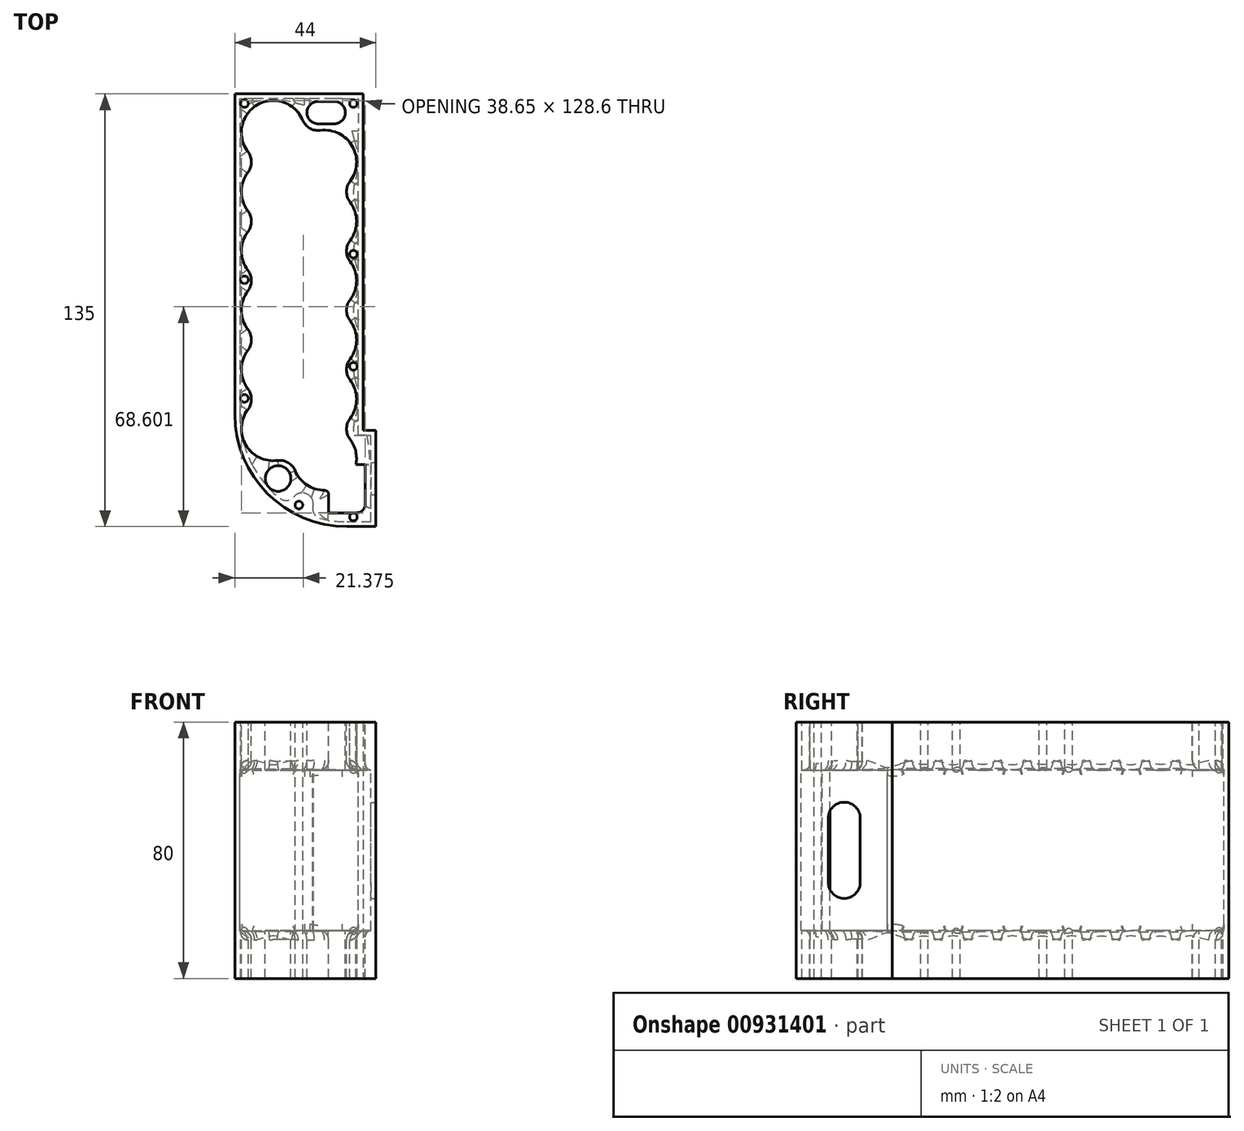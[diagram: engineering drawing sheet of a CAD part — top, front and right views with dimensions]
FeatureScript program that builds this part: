
annotation { "Feature Type Name" : "Feature", "Feature Type Description" : "" }
export const myFeature = defineFeature(function(context is Context, id is Id, definition is map)
    precondition{}
    {
        {
            var Q0;
            Q0=qCreatedBy(makeId("Top.planeOp"),FACE);
            cPlane(context, id + "F0", {"entities" : qUnion([Q0]), "cplaneType" : CPlaneType.OFFSET, "offset" : 40 * mm, "width" : 150 * mm, "height" : 150 * mm});
        }
        {
            var Q0;
            Q0=qCreatedBy(makeId("Top.planeOp"),FACE);
            var sketch = newSketch(context, id + "F1", { "sketchPlane" : qUnion([Q0])});
            skLineSegment(sketch, "E0.right", {"start": v(-40, 0) * mm, "end": v(-40, -100) * mm});
            skPoint(sketch, "E1.visualSharp", {"position": v(-40, -135) * mm});
            skPoint(sketch, "E2.visualSharp", {"position": v(-40, 0) * mm});
            skLineSegment(sketch, "E3", {"start": v(0, 0) * mm, "end": v(0, -105) * mm});
            skLineSegment(sketch, "E4", {"start": v(-40, 0) * mm, "end": v(0, 0) * mm});
            skLineSegment(sketch, "E5.top", {"start": v(0, -105) * mm, "end": v(4, -105) * mm});
            skLineSegment(sketch, "E5.right", {"start": v(4, -135) * mm, "end": v(4, -105) * mm});
            skLineSegment(sketch, "E6", {"start": v(4, -135) * mm, "end": v(-5, -135) * mm});
            skArc(sketch, "E7.filletArc", {"start": v(-40, -100) * mm, "mid": v(-29.75, -124.75) * mm, "end": v(-5, -135) * mm});
            skSolve(sketch);
        }
        {
            var Q0;
            Q0=makeQuery(id+"F1.imprint","IMPRINT",FACE,{"disambiguationData":[TD([[makeQuery(id+"F1.imprint","IMPRINT",EDGE,{"derivedFrom":sQuery(id+"F1.wireOp",EDGE,"E0.right")}),1.0]])]});
            extrude(context, id + "F2", {"entities" : qUnion([Q0]), "depth" : 80 * mm, "offsetDistance" : 25 * mm});
        }
        {
            var Q0;
            Q0=makeQuery(id+"F2.opExtrude","CAP_FACE",FACE,{"disambiguationData":[OSD([sQuery(id+"F1.wireOp",EDGE,"E0.top"),sQuery(id+"F1.wireOp",EDGE,"E0.left"),sQuery(id+"F1.wireOp",EDGE,"E0.right"),sQuery(id+"F1.wireOp",EDGE,"E1.filletArc"),sQuery(id+"F1.wireOp",EDGE,"5de082b1-88c5-4f56-9cd1-09331b00fd2d.trimOffspring"),sQuery(id+"F1.wireOp",EDGE,"y3ADj3GU-friW-LrWS-ZnVf-nILArbpNqqxh"),sQuery(id+"F1.wireOp",EDGE,"uJFoRx8a-Ppp5-qDHF-xN9b-6GK6148I28lK.left"),sQuery(id+"F1.wireOp",EDGE,"uJFoRx8a-Ppp5-qDHF-xN9b-6GK6148I28lK.right"),sQuery(id+"F1.wireOp",EDGE,"b2af3c1e-7181-4fb0-8f65-0e7276eb82ca.trimOffspring"),sQuery(id+"F1.wireOp",EDGE,"7f23342a-69af-42d1-8bd4-2c05ba6568f0.filletArc"),sQuery(id+"F1.wireOp",EDGE,"185a892e-41b9-4107-83af-0d2bc894ce6d.filletArc"),sQuery(id+"F1.wireOp",EDGE,"b194760c-3b3b-4794-9b8b-2c71253df791.filletArc"),sQuery(id+"F1.wireOp",EDGE,"319700d8-119a-4906-a10f-a42b0ff3433d.filletArc"),sQuery(id+"F1.wireOp",EDGE,"ZXkUyEPo-FX4a-Sv19-M192-gNO29ZRSfF8I"),sQuery(id+"F1.wireOp",EDGE,"HvNRA3BX-9FXn-12fZ-Fs24-gRpAAjMtZzFk")])],"isStart":false});
            var sketch = newSketch(context, id + "F3", { "sketchPlane" : qUnion([Q0])});
            skLineSegment(sketch, "E8.2", {"start": v(-37, 0) * mm, "end": v(-37, -100) * mm, "construction": true});
            skPoint(sketch, "E9", {"position": v(-37, -3) * mm});
            skPoint(sketch, "E10", {"position": v(-20, -128.27) * mm});
            skPoint(sketch, "E11", {"position": v(-3, -132) * mm});
            skLineSegment(sketch, "E12.0", {"start": v(-3, 0) * mm, "end": v(-3, -135) * mm, "construction": true});
            skPoint(sketch, "E13", {"position": v(-3, -85) * mm});
            skPoint(sketch, "E14", {"position": v(-3, -50) * mm});
            skPoint(sketch, "E15", {"position": v(-3, -3) * mm});
            skPoint(sketch, "E16", {"position": v(-37, -95) * mm});
            skPoint(sketch, "E17", {"position": v(-37, -58) * mm});
            skArc(sketch, "E18.0", {"start": v(-37, -100) * mm, "mid": v(-27.63, -122.63) * mm, "end": v(-5, -132) * mm, "construction": true});
            skSolve(sketch);
        }
        {
            var Q0;
            Q0=sQuery(id+"F3.wireOp",VERTEX,"E9");
            var Q1;
            Q1=sQuery(id+"F3.wireOp",VERTEX,"f4559d67-b2ce-4cbe-8c48-f7303b728956.direction1.end");
            var Q2;
            Q2=sQuery(id+"F3.wireOp",VERTEX,"666fff49-049b-4152-8810-0d37dc0279b3");
            var Q3;
            Q3=sQuery(id+"F3.wireOp",VERTEX,"E10");
            var Q4;
            Q4=sQuery(id+"F3.wireOp",VERTEX,"E11");
            var Q5;
            Q5=sQuery(id+"F3.wireOp",VERTEX,"E13");
            var Q6;
            Q6=sQuery(id+"F3.wireOp",VERTEX,"E14");
            var Q7;
            Q7=sQuery(id+"F3.wireOp",VERTEX,"E15");
            var Q8;
            Q8=sQuery(id+"F3.wireOp",VERTEX,"E17");
            var Q9;
            Q9=sQuery(id+"F3.wireOp",VERTEX,"E16");
            var Q10;
            Q10=makeQuery(id+"F2.opExtrude","SWEPT_BODY",BODY,{"disambiguationData":[OSD([sQuery(id+"F1.wireOp",EDGE,"E0.top"),sQuery(id+"F1.wireOp",EDGE,"E0.left"),sQuery(id+"F1.wireOp",EDGE,"E0.right"),sQuery(id+"F1.wireOp",EDGE,"E1.filletArc"),sQuery(id+"F1.wireOp",EDGE,"5de082b1-88c5-4f56-9cd1-09331b00fd2d.trimOffspring"),sQuery(id+"F1.wireOp",EDGE,"y3ADj3GU-friW-LrWS-ZnVf-nILArbpNqqxh"),sQuery(id+"F1.wireOp",EDGE,"uJFoRx8a-Ppp5-qDHF-xN9b-6GK6148I28lK.left"),sQuery(id+"F1.wireOp",EDGE,"uJFoRx8a-Ppp5-qDHF-xN9b-6GK6148I28lK.right"),sQuery(id+"F1.wireOp",EDGE,"b2af3c1e-7181-4fb0-8f65-0e7276eb82ca.trimOffspring"),sQuery(id+"F1.wireOp",EDGE,"7f23342a-69af-42d1-8bd4-2c05ba6568f0.filletArc"),sQuery(id+"F1.wireOp",EDGE,"185a892e-41b9-4107-83af-0d2bc894ce6d.filletArc"),sQuery(id+"F1.wireOp",EDGE,"b194760c-3b3b-4794-9b8b-2c71253df791.filletArc"),sQuery(id+"F1.wireOp",EDGE,"319700d8-119a-4906-a10f-a42b0ff3433d.filletArc"),sQuery(id+"F1.wireOp",EDGE,"ZXkUyEPo-FX4a-Sv19-M192-gNO29ZRSfF8I"),sQuery(id+"F1.wireOp",EDGE,"HvNRA3BX-9FXn-12fZ-Fs24-gRpAAjMtZzFk")])]});
            hole(context, id + "F4", {"style" : HoleStyle.SIMPLE, "endStyle" : HoleEndStyle.THROUGH, "holeDiameter" : 2.4 * mm, "majorDiameter" : 5 * mm, "isTappedThrough" : true, "tappedDepth" : 12 * mm, "tapClearance" : 3, "locations" : qUnion([Q0, Q1, Q2, Q3, Q4, Q5, Q6, Q7, Q8, Q9]), "scope" : qUnion([Q10])});
        }
        {
            var Q0;
            Q0=makeQuery(id+"F3.imprint","IMPRINT",FACE,{"disambiguationData":[TD([[makeQuery(id+"F3.imprint","IMPRINT",EDGE,{"derivedFrom":makeQuery(id+"F2.opExtrude","CAP_EDGE",EDGE,{"disambiguationData":[OSD([sQuery(id+"F1.wireOp",EDGE,"E0.right")])],"isStart":false})}),1.0]])]});
            var sketch = newSketch(context, id + "F5", { "sketchPlane" : qUnion([Q0])});
            skArc(sketch, "E19", {"start": v(-19.46, -8.44) * mm, "mid": v(-32.62, -3.99) * mm, "end": v(-35.35, -17.61) * mm});
            skArc(sketch, "E20.1.0.0", {"start": v(-35.35, -24.89) * mm, "mid": v(-37.25, -30.5) * mm, "end": v(-35.35, -36.11) * mm});
            skArc(sketch, "E20.2.0.0", {"start": v(-35.35, -43.39) * mm, "mid": v(-37.25, -49) * mm, "end": v(-35.35, -54.61) * mm});
            skArc(sketch, "E20.3.0.0", {"start": v(-35.35, -61.89) * mm, "mid": v(-37.25, -67.5) * mm, "end": v(-35.35, -73.11) * mm});
            skArc(sketch, "E20.4.0.0", {"start": v(-35.35, -80.39) * mm, "mid": v(-37.25, -86) * mm, "end": v(-35.35, -91.61) * mm});
            skArc(sketch, "E20.5.0.0", {"start": v(-35.35, -98.89) * mm, "mid": v(-36.01, -109.12) * mm, "end": v(-26.82, -113.67) * mm});
            skLineSegment(sketch, "E20.direction1", {"start": v(-28, -12) * mm, "end": v(-28, -30.5) * mm, "construction": true});
            skArc(sketch, "E21", {"start": v(-4.62, -26.86) * mm, "mid": v(-3.97, -16.62) * mm, "end": v(-13.16, -12.08) * mm});
            skArc(sketch, "E22.1.0.0", {"start": v(-4.62, -45.36) * mm, "mid": v(-2.73, -39.75) * mm, "end": v(-4.62, -34.14) * mm});
            skArc(sketch, "E22.2.0.0", {"start": v(-4.62, -63.86) * mm, "mid": v(-2.73, -58.25) * mm, "end": v(-4.62, -52.64) * mm});
            skArc(sketch, "E22.3.0.0", {"start": v(-4.62, -82.36) * mm, "mid": v(-2.73, -76.75) * mm, "end": v(-4.62, -71.14) * mm});
            skArc(sketch, "E22.4.0.0", {"start": v(-4.62, -100.86) * mm, "mid": v(-2.73, -95.25) * mm, "end": v(-4.62, -89.64) * mm});
            skArc(sketch, "E22.5.0.0", {"start": v(-20.51, -117.31) * mm, "mid": v(-17.11, -121.44) * mm, "end": v(-12, -123) * mm});
            skLineSegment(sketch, "E22.direction1", {"start": v(-11.98, -21.25) * mm, "end": v(-11.98, -39.75) * mm, "construction": true});
            skLineSegment(sketch, "E23.bottom", {"start": v(0, -120) * mm, "end": v(-1.56, -120) * mm});
            skLineSegment(sketch, "E23.top", {"start": v(-2, -130) * mm, "end": v(-10, -130) * mm});
            skLineSegment(sketch, "E23.left", {"start": v(0, -120) * mm, "end": v(0, -128) * mm});
            skLineSegment(sketch, "E23.right", {"start": v(-10, -125) * mm, "end": v(-10, -130) * mm});
            skArc(sketch, "E24.trimOffspring", {"start": v(-3.41, -117.24) * mm, "mid": v(-2.8, -112.53) * mm, "end": v(-4.62, -108.14) * mm});
            skPoint(sketch, "E25.visualSharp", {"position": v(-19.99, -16.63) * mm});
            skArc(sketch, "E25.filletArc", {"start": v(-19.46, -8.44) * mm, "mid": v(-16.93, -11.32) * mm, "end": v(-13.16, -12.08) * mm});
            skPoint(sketch, "E26.visualSharp", {"position": v(-28, -21.25) * mm});
            skArc(sketch, "E26.filletArc", {"start": v(-35.35, -24.89) * mm, "mid": v(-34.12, -21.25) * mm, "end": v(-35.35, -17.61) * mm});
            skPoint(sketch, "E27.visualSharp", {"position": v(-28, -39.75) * mm});
            skArc(sketch, "E27.filletArc", {"start": v(-35.35, -43.39) * mm, "mid": v(-34.12, -39.75) * mm, "end": v(-35.35, -36.11) * mm});
            skPoint(sketch, "E28.visualSharp", {"position": v(-28, -58.25) * mm});
            skArc(sketch, "E28.filletArc", {"start": v(-35.35, -61.89) * mm, "mid": v(-34.12, -58.25) * mm, "end": v(-35.35, -54.61) * mm});
            skPoint(sketch, "E29.visualSharp", {"position": v(-28, -76.75) * mm});
            skArc(sketch, "E29.filletArc", {"start": v(-35.35, -80.39) * mm, "mid": v(-34.12, -76.75) * mm, "end": v(-35.35, -73.11) * mm});
            skPoint(sketch, "E30.visualSharp", {"position": v(-11.98, -49) * mm});
            skArc(sketch, "E30.filletArc", {"start": v(-4.62, -45.36) * mm, "mid": v(-5.85, -49) * mm, "end": v(-4.62, -52.64) * mm});
            skPoint(sketch, "E31.visualSharp", {"position": v(-11.98, -30.5) * mm});
            skArc(sketch, "E31.filletArc", {"start": v(-4.62, -26.86) * mm, "mid": v(-5.85, -30.5) * mm, "end": v(-4.62, -34.14) * mm});
            skPoint(sketch, "E32.visualSharp", {"position": v(-11.98, -67.5) * mm});
            skArc(sketch, "E32.filletArc", {"start": v(-4.62, -63.86) * mm, "mid": v(-5.85, -67.5) * mm, "end": v(-4.62, -71.14) * mm});
            skPoint(sketch, "E33.visualSharp", {"position": v(-11.98, -86) * mm});
            skArc(sketch, "E33.filletArc", {"start": v(-4.62, -82.36) * mm, "mid": v(-5.85, -86) * mm, "end": v(-4.62, -89.64) * mm});
            skPoint(sketch, "E34.visualSharp", {"position": v(-11.98, -104.5) * mm});
            skArc(sketch, "E34.filletArc", {"start": v(-4.62, -100.86) * mm, "mid": v(-5.85, -104.5) * mm, "end": v(-4.62, -108.14) * mm});
            skPoint(sketch, "E35.visualSharp", {"position": v(-19.99, -109.12) * mm});
            skArc(sketch, "E35.filletArc", {"start": v(-20.51, -117.31) * mm, "mid": v(-23.05, -114.43) * mm, "end": v(-26.82, -113.67) * mm});
            skPoint(sketch, "E36.visualSharp", {"position": v(-28, -95.25) * mm});
            skArc(sketch, "E36.filletArc", {"start": v(-35.35, -98.89) * mm, "mid": v(-34.12, -95.25) * mm, "end": v(-35.35, -91.61) * mm});
            skPoint(sketch, "E37.visualSharp", {"position": v(0, -130) * mm});
            skArc(sketch, "E37.filletArc", {"start": v(-2, -130) * mm, "mid": v(-0.59, -129.41) * mm, "end": v(0, -128) * mm});
            skPoint(sketch, "E38.visualSharp", {"position": v(-5.16, -120) * mm});
            skArc(sketch, "E38.filletArc", {"start": v(-3.41, -117.24) * mm, "mid": v(-3.22, -119.12) * mm, "end": v(-1.56, -120) * mm});
            skPoint(sketch, "E39.visualSharp", {"position": v(-10, -122.79) * mm});
            skArc(sketch, "E39.filletArc", {"start": v(-10, -125) * mm, "mid": v(-10.58, -123.59) * mm, "end": v(-12, -123) * mm});
            skLineSegment(sketch, "E40", {"start": v(-13.93, -6.12) * mm, "end": v(-8.93, -6.12) * mm});
            skArc(sketch, "E41.0.startCap", {"start": v(-13.93, -9.62) * mm, "mid": v(-17.43, -6.12) * mm, "end": v(-13.93, -2.62) * mm});
            skArc(sketch, "E41.0.endCap", {"start": v(-8.93, -2.62) * mm, "mid": v(-5.43, -6.12) * mm, "end": v(-8.93, -9.62) * mm});
            skLineSegment(sketch, "E41.0.left", {"start": v(-13.93, -2.62) * mm, "end": v(-8.93, -2.62) * mm});
            skLineSegment(sketch, "E41.0.right", {"start": v(-13.93, -9.62) * mm, "end": v(-8.93, -9.62) * mm});
            skSolve(sketch);
        }
        {
            var Q0;
            Q0=makeQuery(id+"F5.imprint","IMPRINT",FACE,{"disambiguationData":[TD([[makeQuery(id+"F5.imprint","IMPRINT",EDGE,{"derivedFrom":sQuery(id+"F5.wireOp",EDGE,"E19")}),1.0]])]});
            extrude(context, id + "F6", {"entities" : qUnion([Q0]), "operationType" : NewBodyOperationType.REMOVE, "oppositeDirection" : true, "depth" : 80 * mm, "offsetDistance" : 25 * mm});
        }
        {
            var Q0;
            Q0=makeQuery(id+"F2.opExtrude","SWEPT_FACE",FACE,{"disambiguationData":[OSD([sQuery(id+"F1.wireOp",EDGE,"E5.right")])]});
            var sketch = newSketch(context, id + "F7", { "sketchPlane" : qUnion([Q0])});
            skLineSegment(sketch, "E42.bottom", {"start": v(-120, 55) * mm, "end": v(-120, 55) * mm});
            skLineSegment(sketch, "E42.top", {"start": v(-120, 25) * mm, "end": v(-120, 25) * mm});
            skLineSegment(sketch, "E42.left", {"start": v(-125, 50) * mm, "end": v(-125, 30) * mm});
            skLineSegment(sketch, "E42.right", {"start": v(-115, 50) * mm, "end": v(-115, 30) * mm});
            skPoint(sketch, "E43.visualSharp", {"position": v(-115, 55) * mm});
            skArc(sketch, "E43.filletArc", {"start": v(-115, 50) * mm, "mid": v(-116.46, 53.54) * mm, "end": v(-120, 55) * mm});
            skPoint(sketch, "E44.visualSharp", {"position": v(-125, 55) * mm});
            skArc(sketch, "E44.filletArc", {"start": v(-120, 55) * mm, "mid": v(-123.54, 53.54) * mm, "end": v(-125, 50) * mm});
            skPoint(sketch, "E45.visualSharp", {"position": v(-125, 25) * mm});
            skArc(sketch, "E45.filletArc", {"start": v(-125, 30) * mm, "mid": v(-123.54, 26.46) * mm, "end": v(-120, 25) * mm});
            skPoint(sketch, "E46.visualSharp", {"position": v(-115, 25) * mm});
            skArc(sketch, "E46.filletArc", {"start": v(-120, 25) * mm, "mid": v(-116.46, 26.46) * mm, "end": v(-115, 30) * mm});
            skSolve(sketch);
        }
        {
            var Q0;
            Q0=makeQuery(id+"F7.imprint","IMPRINT",FACE,{"disambiguationData":[TD([[makeQuery(id+"F7.imprint","IMPRINT",EDGE,{"derivedFrom":sQuery(id+"F7.wireOp",EDGE,"E42.left")}),1.0]])]});
            extrude(context, id + "F8", {"entities" : qUnion([Q0]), "operationType" : NewBodyOperationType.REMOVE, "endBound" : BoundingType.UP_TO_NEXT, "oppositeDirection" : true, "depth" : 25 * mm, "offsetDistance" : 25 * mm});
        }
        {
            var Q0;
            Q0=makeQuery(id+"F3.imprint","IMPRINT",FACE,{"disambiguationData":[TD([[makeQuery(id+"F3.imprint","IMPRINT",EDGE,{"derivedFrom":makeQuery(id+"F2.opExtrude","CAP_EDGE",EDGE,{"disambiguationData":[OSD([sQuery(id+"F1.wireOp",EDGE,"E0.right")])],"isStart":false})}),1.0]])]});
            var sketch = newSketch(context, id + "F9", { "sketchPlane" : qUnion([Q0])});
            skArc(sketch, "E47.0", {"start": v(-18.82, -8.17) * mm, "mid": v(-16.58, -10.71) * mm, "end": v(-13.25, -11.38) * mm});
            skArc(sketch, "E47.1", {"start": v(-4.07, -27.29) * mm, "mid": v(-3.36, -16.27) * mm, "end": v(-13.25, -11.38) * mm});
            skArc(sketch, "E47.2", {"start": v(-4.07, -27.29) * mm, "mid": v(-5.15, -30.5) * mm, "end": v(-4.07, -33.71) * mm});
            skArc(sketch, "E47.3", {"start": v(-4.07, -45.79) * mm, "mid": v(-2.03, -39.75) * mm, "end": v(-4.07, -33.71) * mm});
            skArc(sketch, "E47.4", {"start": v(-4.07, -45.79) * mm, "mid": v(-5.15, -49) * mm, "end": v(-4.07, -52.21) * mm});
            skArc(sketch, "E47.5", {"start": v(-4.07, -64.29) * mm, "mid": v(-2.03, -58.25) * mm, "end": v(-4.07, -52.21) * mm});
            skArc(sketch, "E47.6", {"start": v(-4.07, -64.29) * mm, "mid": v(-5.15, -67.5) * mm, "end": v(-4.07, -70.71) * mm});
            skArc(sketch, "E47.7", {"start": v(-4.07, -82.79) * mm, "mid": v(-2.03, -76.75) * mm, "end": v(-4.07, -70.71) * mm});
            skArc(sketch, "E47.8", {"start": v(-4.07, -82.79) * mm, "mid": v(-5.15, -86) * mm, "end": v(-4.07, -89.21) * mm});
            skArc(sketch, "E47.9", {"start": v(-35.91, -98.46) * mm, "mid": v(-36.62, -109.47) * mm, "end": v(-26.73, -114.37) * mm});
            skArc(sketch, "E47.10", {"start": v(-35.91, -98.46) * mm, "mid": v(-34.82, -95.25) * mm, "end": v(-35.91, -92.04) * mm});
            skArc(sketch, "E47.11", {"start": v(-35.91, -79.96) * mm, "mid": v(-37.95, -86) * mm, "end": v(-35.91, -92.04) * mm});
            skArc(sketch, "E47.12", {"start": v(-35.91, -79.96) * mm, "mid": v(-34.82, -76.75) * mm, "end": v(-35.91, -73.54) * mm});
            skArc(sketch, "E47.13", {"start": v(-35.91, -61.46) * mm, "mid": v(-37.95, -67.5) * mm, "end": v(-35.91, -73.54) * mm});
            skArc(sketch, "E47.14", {"start": v(-35.91, -61.46) * mm, "mid": v(-34.82, -58.25) * mm, "end": v(-35.91, -55.04) * mm});
            skArc(sketch, "E47.15", {"start": v(-35.91, -24.46) * mm, "mid": v(-34.82, -21.25) * mm, "end": v(-35.91, -18.04) * mm});
            skArc(sketch, "E47.16", {"start": v(-35.91, -24.46) * mm, "mid": v(-37.95, -30.5) * mm, "end": v(-35.91, -36.54) * mm});
            skArc(sketch, "E47.17", {"start": v(-35.91, -42.96) * mm, "mid": v(-34.82, -39.75) * mm, "end": v(-35.91, -36.54) * mm});
            skArc(sketch, "E47.18", {"start": v(-35.91, -42.96) * mm, "mid": v(-37.95, -49) * mm, "end": v(-35.91, -55.04) * mm});
            skArc(sketch, "E47.19", {"start": v(-21.16, -117.58) * mm, "mid": v(-23.4, -115.04) * mm, "end": v(-26.73, -114.37) * mm});
            skArc(sketch, "E47.20", {"start": v(-21.16, -117.58) * mm, "mid": v(-17.5, -122.03) * mm, "end": v(-12, -123.7) * mm});
            skArc(sketch, "E47.21", {"start": v(-10.7, -125) * mm, "mid": v(-11.08, -124.08) * mm, "end": v(-12, -123.7) * mm});
            skLineSegment(sketch, "E47.22", {"start": v(-10.7, -125) * mm, "end": v(-10.7, -130.7) * mm});
            skLineSegment(sketch, "E47.23", {"start": v(-2, -130.7) * mm, "end": v(-10.7, -130.7) * mm});
            skArc(sketch, "E47.24", {"start": v(-2, -130.7) * mm, "mid": v(-0.1, -129.9) * mm, "end": v(0.7, -128) * mm});
            skLineSegment(sketch, "E47.25", {"start": v(0.7, -115.7) * mm, "end": v(0.7, -128) * mm});
            skArc(sketch, "E47.28", {"start": v(-18.82, -8.17) * mm, "mid": v(-32.97, -3.38) * mm, "end": v(-35.91, -18.04) * mm});
            skArc(sketch, "E47.29", {"start": v(-2.22, -115.7) * mm, "mid": v(-2.28, -111.5) * mm, "end": v(-4.07, -107.71) * mm});
            skArc(sketch, "E47.30", {"start": v(-4.07, -101.29) * mm, "mid": v(-5.15, -104.5) * mm, "end": v(-4.07, -107.71) * mm});
            skArc(sketch, "E47.31", {"start": v(-4.07, -101.29) * mm, "mid": v(-2.03, -95.25) * mm, "end": v(-4.07, -89.21) * mm});
            skLineSegment(sketch, "E48", {"start": v(0.7, -115.7) * mm, "end": v(-2.22, -115.7) * mm});
            skSolve(sketch);
        }
        {
            var Q0;
            Q0=makeQuery(id+"F9.imprint","IMPRINT",FACE,{"disambiguationData":[TD([[makeQuery(id+"F9.imprint","IMPRINT",EDGE,{"derivedFrom":sQuery(id+"F9.wireOp",EDGE,"E47.0")}),-1.0]])]});
            extrude(context, id + "F10", {"entities" : qUnion([Q0]), "operationType" : NewBodyOperationType.REMOVE, "oppositeDirection" : true, "depth" : 80 * mm, "offsetDistance" : 25 * mm});
        }
        {
            var Q0;
            Q0=makeQuery(id+"F3.imprint","IMPRINT",FACE,{"disambiguationData":[TD([[makeQuery(id+"F3.imprint","IMPRINT",EDGE,{"derivedFrom":makeQuery(id+"F2.opExtrude","CAP_EDGE",EDGE,{"disambiguationData":[OSD([sQuery(id+"F1.wireOp",EDGE,"E0.right")])],"isStart":false})}),1.0]])]});
            var sketch = newSketch(context, id + "F11", { "sketchPlane" : qUnion([Q0])});
            skLineSegment(sketch, "E49", {"start": v(-14, -5.82) * mm, "end": v(-9, -5.82) * mm});
            skArc(sketch, "E50.0.startCap", {"start": v(-14, -9.32) * mm, "mid": v(-17.5, -5.82) * mm, "end": v(-14, -2.32) * mm});
            skArc(sketch, "E50.0.endCap", {"start": v(-9, -2.32) * mm, "mid": v(-5.5, -5.82) * mm, "end": v(-9, -9.32) * mm});
            skLineSegment(sketch, "E50.0.left", {"start": v(-14, -2.32) * mm, "end": v(-9, -2.32) * mm});
            skLineSegment(sketch, "E50.0.right", {"start": v(-14, -9.32) * mm, "end": v(-9, -9.32) * mm});
            skCircle(sketch, "E51", {"center": v(-26.5, -120) * mm, "radius": 4 * mm});
            skSolve(sketch);
        }
        {
            var Q0;
            Q0 = qSketchRegion(id + "F11", true);
            extrude(context, id + "F12", {"entities" : qUnion([Q0]), "operationType" : NewBodyOperationType.REMOVE, "endBound" : BoundingType.UP_TO_NEXT, "oppositeDirection" : true, "depth" : 25 * mm, "offsetDistance" : 25 * mm});
        }
        {
            var Q0;
            Q0=qCreatedBy(id+"F0.planeOp",FACE);
            var sketch = newSketch(context, id + "F13", { "sketchPlane" : qUnion([Q0])});
            skLineSegment(sketch, "E52.0", {"start": v(-38.5, -1.5) * mm, "end": v(-1.5, -1.5) * mm});
            skLineSegment(sketch, "E52.1", {"start": v(-38.5, -1.5) * mm, "end": v(-38.5, -100) * mm});
            skLineSegment(sketch, "E52.2", {"start": v(-1.5, -106.5) * mm, "end": v(2.5, -106.5) * mm});
            skLineSegment(sketch, "E52.3", {"start": v(2.5, -133.5) * mm, "end": v(2.5, -106.5) * mm});
            skLineSegment(sketch, "E52.4", {"start": v(2.5, -133.5) * mm, "end": v(-5, -133.5) * mm});
            skLineSegment(sketch, "E52.5", {"start": v(-1.5, -1.5) * mm, "end": v(-1.5, -106.5) * mm});
            skArc(sketch, "E52.6", {"start": v(-38.5, -100) * mm, "mid": v(-35.18, -114.54) * mm, "end": v(-25.88, -126.2) * mm});
            skArc(sketch, "E53", {"start": v(-15.6, -128.82) * mm, "mid": v(-17.43, -124.87) * mm, "end": v(-21.7, -125.77) * mm});
            skArc(sketch, "E54.trimOffspring", {"start": v(-13.43, -132.42) * mm, "mid": v(-9.25, -133.23) * mm, "end": v(-5, -133.5) * mm});
            skPoint(sketch, "E55.visualSharp", {"position": v(-17.4, -131.12) * mm});
            skArc(sketch, "E55.filletArc", {"start": v(-15.6, -128.82) * mm, "mid": v(-15.25, -131.06) * mm, "end": v(-13.43, -132.42) * mm});
            skPoint(sketch, "E56.visualSharp", {"position": v(-22.45, -128.6) * mm});
            skArc(sketch, "E56.filletArc", {"start": v(-25.88, -126.2) * mm, "mid": v(-23.7, -126.84) * mm, "end": v(-21.7, -125.77) * mm});
            skSolve(sketch);
        }
        {
            var Q0;
            Q0 = qSketchRegion(id + "F13", true);
            extrude(context, id + "F14", {"entities" : qUnion([Q0]), "operationType" : NewBodyOperationType.REMOVE, "oppositeDirection" : true, "depth" : 25 * mm, "offsetDistance" : 25 * mm, "hasSecondDirection" : true, "secondDirectionOppositeDirection" : false, "secondDirectionDepth" : 25 * mm});
        }
        {
            var Q0;
            Q0=makeQuery(id+"F14.boolean.opBoolean","INTERSECT",EDGE,{"derivedFrom":[makeQuery(id+"F10.boolean.opBoolean","COPY",FACE,{"derivedFrom":makeQuery(id+"F10.opExtrude","SWEPT_FACE",FACE,{"disambiguationData":[OSD([sQuery(id+"F9.wireOp",EDGE,"E47.13")])]})}),makeQuery(id+"F14.opExtrude","CAP_FACE",FACE,{"disambiguationData":[OSD([sQuery(id+"F13.wireOp",EDGE,"E52.0"),sQuery(id+"F13.wireOp",EDGE,"E52.1"),sQuery(id+"F13.wireOp",EDGE,"E52.2"),sQuery(id+"F13.wireOp",EDGE,"E52.3"),sQuery(id+"F13.wireOp",EDGE,"E52.4"),sQuery(id+"F13.wireOp",EDGE,"E52.5"),sQuery(id+"F13.wireOp",EDGE,"E52.6")])],"isStart":false})]});
            var Q1;
            Q1=makeQuery(id+"F14.boolean.opBoolean","INTERSECT",EDGE,{"derivedFrom":[makeQuery(id+"F10.boolean.opBoolean","COPY",FACE,{"derivedFrom":makeQuery(id+"F10.opExtrude","SWEPT_FACE",FACE,{"disambiguationData":[OSD([sQuery(id+"F9.wireOp",EDGE,"E47.13")])]})}),makeQuery(id+"F14.opExtrude","CAP_FACE",FACE,{"disambiguationData":[OSD([sQuery(id+"F13.wireOp",EDGE,"E52.0"),sQuery(id+"F13.wireOp",EDGE,"E52.1"),sQuery(id+"F13.wireOp",EDGE,"E52.2"),sQuery(id+"F13.wireOp",EDGE,"E52.3"),sQuery(id+"F13.wireOp",EDGE,"E52.4"),sQuery(id+"F13.wireOp",EDGE,"E52.5"),sQuery(id+"F13.wireOp",EDGE,"E52.6")])],"isStart":true})]});
            fillet(context, id + "F15", {"entities" : qUnion([Q0, Q1]), "radius" : 3 * mm, "tangentPropagation" : true, "allowEdgeOverflow" : false});
        }
        {
            var Q0;
            Q0=makeQuery(id+"F14.boolean.opBoolean","INTERSECT",EDGE,{"derivedFrom":[makeQuery(id+"F10.boolean.opBoolean","COPY",FACE,{"derivedFrom":makeQuery(id+"F10.opExtrude","SWEPT_FACE",FACE,{"disambiguationData":[OSD([sQuery(id+"F9.wireOp",EDGE,"E47.23")])]})}),makeQuery(id+"F14.opExtrude","CAP_FACE",FACE,{"disambiguationData":[OSD([sQuery(id+"F13.wireOp",EDGE,"E52.0"),sQuery(id+"F13.wireOp",EDGE,"E52.1"),sQuery(id+"F13.wireOp",EDGE,"E52.2"),sQuery(id+"F13.wireOp",EDGE,"E52.3"),sQuery(id+"F13.wireOp",EDGE,"E52.4"),sQuery(id+"F13.wireOp",EDGE,"E52.5"),sQuery(id+"F13.wireOp",EDGE,"E52.6")])],"isStart":false})]});
            var Q1;
            Q1=makeQuery(id+"F14.boolean.opBoolean","INTERSECT",EDGE,{"derivedFrom":[makeQuery(id+"F10.boolean.opBoolean","COPY",FACE,{"derivedFrom":makeQuery(id+"F10.opExtrude","SWEPT_FACE",FACE,{"disambiguationData":[OSD([sQuery(id+"F9.wireOp",EDGE,"E47.23")])]})}),makeQuery(id+"F14.opExtrude","CAP_FACE",FACE,{"disambiguationData":[OSD([sQuery(id+"F13.wireOp",EDGE,"E52.0"),sQuery(id+"F13.wireOp",EDGE,"E52.1"),sQuery(id+"F13.wireOp",EDGE,"E52.2"),sQuery(id+"F13.wireOp",EDGE,"E52.3"),sQuery(id+"F13.wireOp",EDGE,"E52.4"),sQuery(id+"F13.wireOp",EDGE,"E52.5"),sQuery(id+"F13.wireOp",EDGE,"E52.6")])],"isStart":true})]});
            fillet(context, id + "F16", {"entities" : qUnion([Q0, Q1]), "radius" : 2 * mm, "tangentPropagation" : true, "allowEdgeOverflow" : false});
        }
        {
            var Q0;
            Q0=makeQuery(id+"F14.boolean.opBoolean","COPY",EDGE,{"derivedFrom":makeQuery(id+"F14.opExtrude","CAP_EDGE",EDGE,{"disambiguationData":[OSD([sQuery(id+"F13.wireOp",EDGE,"E52.0")])],"isStart":false})});
            var Q1;
            Q1=makeQuery(id+"F14.boolean.opBoolean","COPY",EDGE,{"derivedFrom":makeQuery(id+"F14.opExtrude","CAP_EDGE",EDGE,{"disambiguationData":[OSD([sQuery(id+"F13.wireOp",EDGE,"E52.5")])],"isStart":false})});
            var Q2;
            Q2=makeQuery(id+"F14.boolean.opBoolean","COPY",EDGE,{"derivedFrom":makeQuery(id+"F14.opExtrude","CAP_EDGE",EDGE,{"disambiguationData":[OSD([sQuery(id+"F13.wireOp",EDGE,"E52.0")])],"isStart":true})});
            var Q3;
            Q3=makeQuery(id+"F14.boolean.opBoolean","COPY",EDGE,{"derivedFrom":makeQuery(id+"F14.opExtrude","CAP_EDGE",EDGE,{"disambiguationData":[OSD([sQuery(id+"F13.wireOp",EDGE,"E52.5")])],"isStart":true})});
            fillet(context, id + "F17", {"entities" : qUnion([Q0, Q1, Q2, Q3]), "radius" : 2 * mm, "tangentPropagation" : true, "allowEdgeOverflow" : false});
        }
    });
